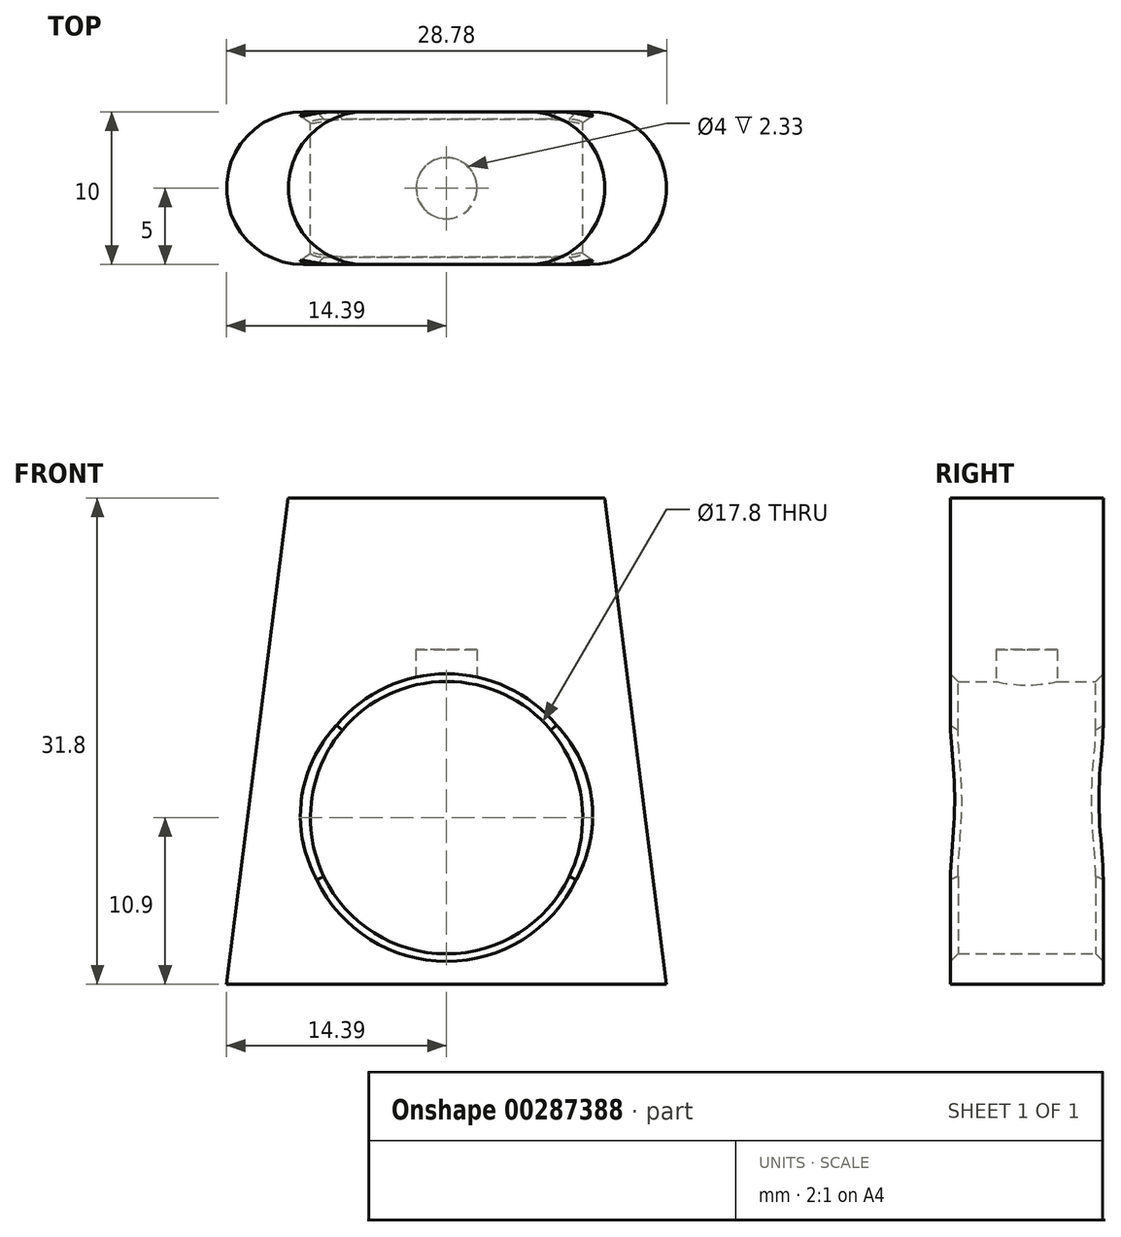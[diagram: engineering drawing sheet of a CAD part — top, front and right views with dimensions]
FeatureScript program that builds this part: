
annotation { "Feature Type Name" : "Feature", "Feature Type Description" : "" }
export const myFeature = defineFeature(function(context is Context, id is Id, definition is map)
    precondition{}
    {
        {
            var Q0;
            Q0=qCreatedBy(makeId("Front.planeOp"),FACE);
            var sketch = newSketch(context, id + "F0", { "sketchPlane" : qUnion([Q0])});
            skCircle(sketch, "E0", {"center": v(0, 0) * mm, "radius": 8.9 * mm});
            skLineSegment(sketch, "E1", {"start": v(-10.35, 20.9) * mm, "end": v(-14.39, -10.9) * mm});
            skLineSegment(sketch, "E2", {"start": v(-14.39, -10.9) * mm, "end": v(0, -10.9) * mm});
            skLineSegment(sketch, "E3", {"start": v(-10.35, 20.9) * mm, "end": v(0, 20.9) * mm});
            skLineSegment(sketch, "E4.MirrorCS", {"start": v(10.35, 20.9) * mm, "end": v(0, 20.9) * mm});
            skLineSegment(sketch, "E5.MirrorCS", {"start": v(10.35, 20.9) * mm, "end": v(14.39, -10.9) * mm});
            skLineSegment(sketch, "E6.MirrorCS", {"start": v(14.39, -10.9) * mm, "end": v(0, -10.9) * mm});
            skSolve(sketch);
        }
        {
            var Q0;
            Q0=makeQuery(id+"F0.imprint","IMPRINT",FACE,{"disambiguationData":[TD([[makeQuery(id+"F0.imprint","IMPRINT",EDGE,{"derivedFrom":sQuery(id+"F0.wireOp",EDGE,"E0")}),-1.0]])]});
            extrude(context, id + "F1", {"entities" : qUnion([Q0]), "depth" : 5 * mm, "hasSecondDirection" : true, "secondDirectionOppositeDirection" : true, "secondDirectionDepth" : 5 * mm});
        }
        {
            var Q0;
            Q0=makeQuery(id+"F1.opExtrude","CAP_EDGE",EDGE,{"disambiguationData":[OSD([sQuery(id+"F0.wireOp",EDGE,"E5.MirrorCS")])],"isStart":false});
            var Q1;
            Q1=makeQuery(id+"F1.opExtrude","CAP_EDGE",EDGE,{"disambiguationData":[OSD([sQuery(id+"F0.wireOp",EDGE,"E5.MirrorCS")])],"isStart":true});
            var Q2;
            Q2=makeQuery(id+"F1.opExtrude","CAP_EDGE",EDGE,{"disambiguationData":[OSD([sQuery(id+"F0.wireOp",EDGE,"E1")])],"isStart":false});
            var Q3;
            Q3=makeQuery(id+"F1.opExtrude","CAP_EDGE",EDGE,{"disambiguationData":[OSD([sQuery(id+"F0.wireOp",EDGE,"E1")])],"isStart":true});
            fillet(context, id + "F2", {"entities" : qUnion([Q0, Q1, Q2, Q3]), "radius" : 5 * mm, "tangentPropagation" : true, "allowEdgeOverflow" : false});
        }
        {
            var Q0;
            Q0=makeQuery(id+"F1.opExtrude","CAP_EDGE",EDGE,{"disambiguationData":[OSD([sQuery(id+"F0.wireOp",EDGE,"E0")])],"isStart":false});
            var Q1;
            Q1=makeQuery(id+"F1.opExtrude","CAP_EDGE",EDGE,{"disambiguationData":[OSD([sQuery(id+"F0.wireOp",EDGE,"E0")])],"isStart":true});
            chamfer(context, id + "F3", {"entities" : qUnion([Q0, Q1]), "width" : .5 * mm, "tangentPropagation" : true});
        }
        {
            var Q0;
            Q0=qCreatedBy(makeId("Top.planeOp"),FACE);
            var sketch = newSketch(context, id + "F4", { "sketchPlane" : qUnion([Q0])});
            skCircle(sketch, "E7", {"center": v(0, 0) * mm, "radius": 2 * mm});
            skSolve(sketch);
        }
        {
            var Q0;
            Q0=makeQuery(id+"F4.imprint","IMPRINT",FACE,{"disambiguationData":[TD([[makeQuery(id+"F4.imprint","IMPRINT",EDGE,{"derivedFrom":sQuery(id+"F4.wireOp",EDGE,"E7")}),1.0]])]});
            extrude(context, id + "F5", {"entities" : qUnion([Q0]), "operationType" : NewBodyOperationType.REMOVE, "depth" : 11 * mm});
        }
    });
